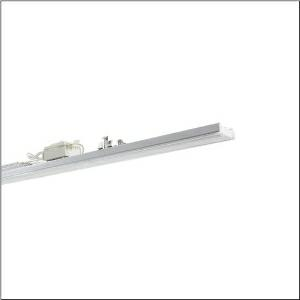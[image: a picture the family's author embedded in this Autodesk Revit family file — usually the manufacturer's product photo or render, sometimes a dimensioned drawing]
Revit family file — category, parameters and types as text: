
# Revit family: licross_21_recessed_mo_52tl18dv46xgd
name_source: partatom
category: Lighting Fixtures
units: mm (PartAtom-declared; Revit-internal decimal feet)

## family parameters
Cut with Voids When Loaded = No
Host = Face
Light Source = No
Part Type = Normal
Room Calculation Point = No
Round Connector Dimension = Use Diameter
Shared = No

## types (1)
- --- (1 x LED, 940 lm, 4.6 W, 4000K)
    Apparent Load = 5 VA
    CIE Flux Codes = 79 95 99 100 100
    Color Rendering = 80
    Color Temperature = 4000K
    Default Elevation = 1800 mm
    Description = Licross 21 Recessed MO, luminaire insert, of sheet steel, galvanised, coil coated, white, length: 2.250mm, width: 66mm, height: 67mm, LED rated luminous flux: 6.200lm, light colour: 840, SDCM (Standard Deviation of Colour Matching)MacAdam ≤ 3 SDCM (initial), control gear: DALI 2 (for two DALI lines), with plug, 5-pole, with phase selection, mains connection: 220..240V, AC/DC, 0/50..60Hz, rated input power: 35W, internal wiring halogen-free, for central battery installations according to EN 60598-2-22, for emergency light function, without changeover relay, primary light control with lens, of plastic, primary optical cover: cover, of PMMA, light emission: direct distribution, primary light characteristic: symmetric, protection rating (complete): IP40, insulation class (complete): insulation class I (protective earthing), certification: CE, ENEC, VDE, UKCA, protection symbol: D if used in an environment without relevant dust loads with corresponding accessories, impact resistance: IK06, permissible ambient temperature for indoor applications: -25..+45°C, standard: EN 60598-2-22, corresponds to IFS (International Featured Standards) requirements for safety and quality in the food industry, reducing of maximum allowable ambient temperature of 5°C with ceiling mounting, LABS conformity tested according to VDMA 24364:2018-05, The light source and the operating device comply with the requirements of the Ecodesign Regulation (EU) 2019/2020 and are replaceable in accordance with this regulation, packaging unit: 1 piece
    Height = 58 mm
    Lamp = 1 x LED
    Lamp Light Flux = 940 lm
    Lamp Power = 4.6 W
    Lamp count = 1
    Length = 2250 mm
    Luminous efficacy = 204 lm/W
    Manufacturer = Siteco
    ModVariant = No
    Model = 52TL18DV46XGD
    Mounting Place = Ceiling
    Mounting Type = Pendant
    Number of Poles = 1
    OnlyDefault = Yes
    Power Factor = 1
    Product Name = Licross 21 Recessed MO
    Product group = luminaire insert | ceiling pendant
    ProductGroupID = 901
    Protection Class = Protection class I
    Protection Degree = IP 40
    RLX_Detail_Level = 1
    RLX_Emergency_Light_Flux = 0 lm
    RLX_Emergency_Type = 0
    RLX_Emergency_Type_DB = No
    RlxData = <blob elided: 29457 chars, md5=d89c2288>
    Socket = socket
    Standby Power = 0 W
    System Light Flux = 940 lm
    System Power = 5 W
    Type Comments = : DC mode (central or group accumulator) initial emergency light level
    Type Image = l_1296930.jpg
    URL = http://relux.com
    VarID = @adj_048351
    Voltage = 0 V
    Weight = 0.00 kg
    Width = 66 mm

## geometry (parser evidence)
native form markers: Blend x4, Sweep x9
no freeform markers — native parametric forms only
